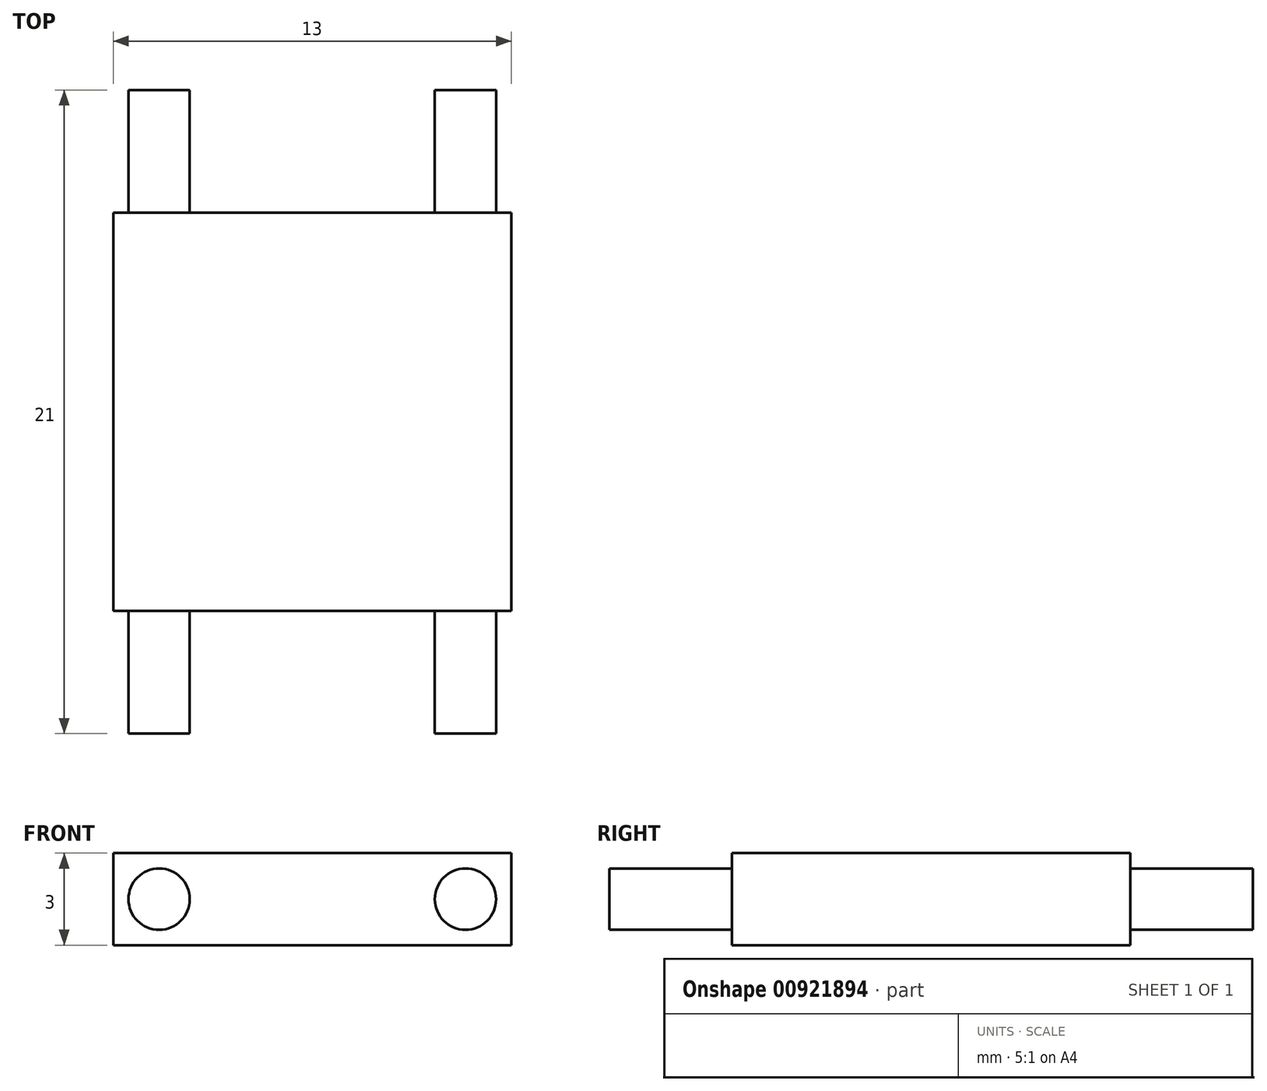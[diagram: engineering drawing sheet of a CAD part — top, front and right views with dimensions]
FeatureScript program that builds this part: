
annotation { "Feature Type Name" : "Feature", "Feature Type Description" : "" }
export const myFeature = defineFeature(function(context is Context, id is Id, definition is map)
    precondition{}
    {
        {
            var Q0;
            Q0=qCreatedBy(makeId("Top.planeOp"),FACE);
            var sketch = newSketch(context, id + "F0", { "sketchPlane" : qUnion([Q0])});
            skLineSegment(sketch, "E0.bottom", {"start": v(0, 0) * mm, "end": v(13, 0) * mm});
            skLineSegment(sketch, "E0.top", {"start": v(0, 13) * mm, "end": v(13, 13) * mm});
            skLineSegment(sketch, "E0.left", {"start": v(0, 0) * mm, "end": v(0, 13) * mm});
            skLineSegment(sketch, "E0.right", {"start": v(13, 0) * mm, "end": v(13, 13) * mm});
            skSolve(sketch);
        }
        {
            var Q0;
            Q0=makeQuery(id+"F0.imprint","IMPRINT",FACE,{"disambiguationData":[TD([[makeQuery(id+"F0.imprint","IMPRINT",EDGE,{"derivedFrom":sQuery(id+"F0.wireOp",EDGE,"E0.bottom")}),1.0]])]});
            extrude(context, id + "F1", {"entities" : qUnion([Q0]), "depth" : 3 * mm, "offsetDistance" : 25 * mm});
        }
        {
            var Q0;
            Q0=makeQuery(id+"F1.opExtrude","SWEPT_FACE",FACE,{"disambiguationData":[OSD([sQuery(id+"F0.wireOp",EDGE,"E0.bottom")])]});
            var sketch = newSketch(context, id + "F2", { "sketchPlane" : qUnion([Q0])});
            skCircle(sketch, "E1", {"center": v(1.5, 1.5) * mm, "radius": 1 * mm});
            skCircle(sketch, "E2", {"center": v(11.5, 1.5) * mm, "radius": 1 * mm});
            skSolve(sketch);
        }
        {
            var Q0;
            Q0=makeQuery(id+"F2.imprint","IMPRINT",FACE,{"disambiguationData":[TD([[makeQuery(id+"F2.imprint","IMPRINT",EDGE,{"derivedFrom":sQuery(id+"F2.wireOp",EDGE,"E1")}),1.0]])]});
            var Q1;
            Q1=makeQuery(id+"F2.imprint","IMPRINT",FACE,{"disambiguationData":[TD([[makeQuery(id+"F2.imprint","IMPRINT",EDGE,{"derivedFrom":sQuery(id+"F2.wireOp",EDGE,"E2")}),1.0]])]});
            extrude(context, id + "F3", {"entities" : qUnion([Q0, Q1]), "operationType" : NewBodyOperationType.ADD, "depth" : 4 * mm, "offsetDistance" : 25 * mm});
        }
        {
            var Q0;
            Q0=makeQuery(id+"F1.opExtrude","SWEPT_FACE",FACE,{"disambiguationData":[OSD([sQuery(id+"F0.wireOp",EDGE,"E0.top")])]});
            var sketch = newSketch(context, id + "F4", { "sketchPlane" : qUnion([Q0])});
            skCircle(sketch, "E3", {"center": v(-11.5, 1.5) * mm, "radius": 1 * mm});
            skCircle(sketch, "E4", {"center": v(-1.5, 1.5) * mm, "radius": 1 * mm});
            skSolve(sketch);
        }
        {
            var Q0;
            Q0=makeQuery(id+"F4.imprint","IMPRINT",FACE,{"disambiguationData":[TD([[makeQuery(id+"F4.imprint","IMPRINT",EDGE,{"derivedFrom":sQuery(id+"F4.wireOp",EDGE,"E3")}),1.0]])]});
            var Q1;
            Q1=makeQuery(id+"F4.imprint","IMPRINT",FACE,{"disambiguationData":[TD([[makeQuery(id+"F4.imprint","IMPRINT",EDGE,{"derivedFrom":sQuery(id+"F4.wireOp",EDGE,"E4")}),1.0]])]});
            extrude(context, id + "F5", {"entities" : qUnion([Q0, Q1]), "operationType" : NewBodyOperationType.ADD, "depth" : 4 * mm, "offsetDistance" : 25 * mm});
        }
    });
